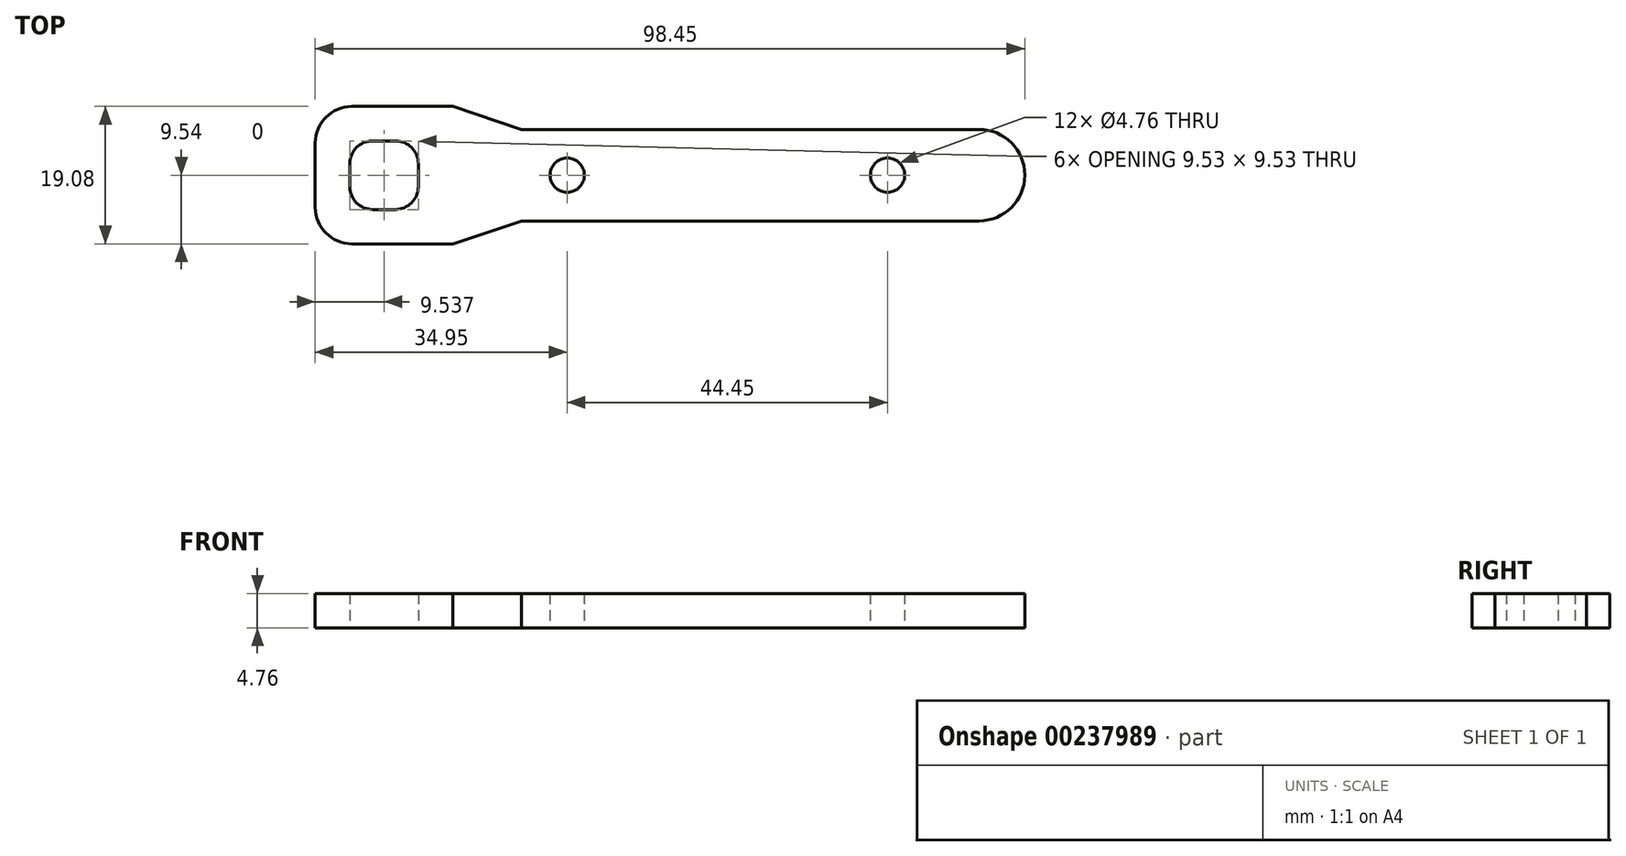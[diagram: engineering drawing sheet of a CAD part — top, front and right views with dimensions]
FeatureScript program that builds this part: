
annotation { "Feature Type Name" : "Feature", "Feature Type Description" : "" }
export const myFeature = defineFeature(function(context is Context, id is Id, definition is map)
    precondition{}
    {
        {
            var Q0;
            Q0=qCreatedBy(makeId("Top.planeOp"),FACE);
            var sketch = newSketch(context, id + "F0", { "sketchPlane" : qUnion([Q0])});
            skLineSegment(sketch, "E0.bottom", {"start": v(-6.35, 6.35) * mm, "end": v(-69.85, 6.35) * mm});
            skLineSegment(sketch, "E0.top", {"start": v(-6.35, -6.35) * mm, "end": v(-69.85, -6.35) * mm});
            skLineSegment(sketch, "E1", {"start": v(0, 0) * mm, "end": v(-79.38, 0) * mm, "construction": true});
            skCircle(sketch, "E2", {"center": v(-19.05, 0) * mm, "radius": 2.38 * mm});
            skCircle(sketch, "E3", {"center": v(-63.5, 0) * mm, "radius": 2.38 * mm});
            skPoint(sketch, "E4.orphan", {"position": v(0, 6.35) * mm});
            skPoint(sketch, "E5.orphan", {"position": v(0, -6.35) * mm});
            skArc(sketch, "E6", {"start": v(-6.35, 6.35) * mm, "mid": v(0, 0) * mm, "end": v(-6.35, -6.35) * mm});
            skLineSegment(sketch, "E7.bottom", {"start": v(-79.38, 9.54) * mm, "end": v(-98.45, 9.54) * mm});
            skLineSegment(sketch, "E7.top", {"start": v(-79.38, -9.54) * mm, "end": v(-98.45, -9.54) * mm});
            skLineSegment(sketch, "E7.right", {"start": v(-98.45, 9.54) * mm, "end": v(-98.45, -9.54) * mm});
            skPoint(sketch, "E7.middle", {"position": v(-88.91, 0) * mm});
            skLineSegment(sketch, "E8.bottom", {"start": v(-84.15, 4.76) * mm, "end": v(-93.68, 4.76) * mm});
            skLineSegment(sketch, "E8.top", {"start": v(-84.15, -4.76) * mm, "end": v(-93.68, -4.76) * mm});
            skLineSegment(sketch, "E8.left", {"start": v(-84.15, 4.76) * mm, "end": v(-84.15, -4.76) * mm});
            skLineSegment(sketch, "E8.right", {"start": v(-93.68, 4.76) * mm, "end": v(-93.68, -4.76) * mm});
            skLineSegment(sketch, "E9", {"start": v(-79.38, 9.54) * mm, "end": v(-69.85, 6.35) * mm});
            skLineSegment(sketch, "E10", {"start": v(-79.38, -9.54) * mm, "end": v(-69.85, -6.35) * mm});
            skPoint(sketch, "E11.orphan", {"position": v(-79.38, 6.35) * mm});
            skPoint(sketch, "E12.orphan", {"position": v(-79.38, -6.35) * mm});
            skSolve(sketch);
        }
        {
            var Q0;
            Q0=qSketchRegion(id+"F0",true);
            extrude(context, id + "F1", {"entities" : qUnion([Q0]), "depth" : 4.76 * mm});
        }
        {
            var Q0;
            Q0=makeQuery(id+"F1.opExtrude","SWEPT_EDGE",EDGE,{"disambiguationData":[OSD([sQuery(id+"F0.wireOp",EDGE,"E7.bottom"),sQuery(id+"F0.wireOp",EDGE,"E7.right")])]});
            var Q1;
            Q1=makeQuery(id+"F1.opExtrude","SWEPT_EDGE",EDGE,{"disambiguationData":[OSD([sQuery(id+"F0.wireOp",EDGE,"E7.top"),sQuery(id+"F0.wireOp",EDGE,"E7.right")])]});
            fillet(context, id + "F2", {"entities" : qUnion([Q0, Q1]), "radius" : 5.08 * mm, "tangentPropagation" : true, "allowEdgeOverflow" : false});
        }
        {
            var Q0;
            Q0=makeQuery(id+"F1.opExtrude","SWEPT_EDGE",EDGE,{"disambiguationData":[OSD([sQuery(id+"F0.wireOp",EDGE,"E8.top"),sQuery(id+"F0.wireOp",EDGE,"E8.left")])]});
            var Q1;
            Q1=makeQuery(id+"F1.opExtrude","SWEPT_EDGE",EDGE,{"disambiguationData":[OSD([sQuery(id+"F0.wireOp",EDGE,"E8.bottom"),sQuery(id+"F0.wireOp",EDGE,"E8.left")])]});
            var Q2;
            Q2=makeQuery(id+"F1.opExtrude","SWEPT_EDGE",EDGE,{"disambiguationData":[OSD([sQuery(id+"F0.wireOp",EDGE,"E8.bottom"),sQuery(id+"F0.wireOp",EDGE,"E8.right")])]});
            var Q3;
            Q3=makeQuery(id+"F1.opExtrude","SWEPT_EDGE",EDGE,{"disambiguationData":[OSD([sQuery(id+"F0.wireOp",EDGE,"E8.top"),sQuery(id+"F0.wireOp",EDGE,"E8.right")])]});
            fillet(context, id + "F3", {"entities" : qUnion([Q0, Q1, Q2, Q3]), "radius" : 3.17 * mm, "tangentPropagation" : true, "allowEdgeOverflow" : false});
        }
    });
